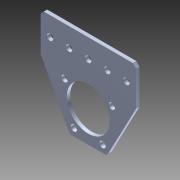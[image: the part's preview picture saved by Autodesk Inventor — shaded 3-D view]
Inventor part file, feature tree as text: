
AUTODESK INVENTOR PART (.ipt)
format: ipt  version: 2014 SP1 (Build 180222100, 222)  size: 152,576 bytes
history: native  units: in
note: dims shown in document units (in); Inventor stores cm internally (conversion verified against a paired STEP export)
features: other x2, sketch x1, imported_body x1
ambient origin geometry x8: Origin, YZ Plane, XZ Plane, XY Plane, X Axis, Y Axis, Z Axis, Center Point
bodies: Body1 (feature_tree)
feature tree (4):
  other  "Cut-Extrude1"
  other  "217-3553-STEP1"
  sketch  "Sketch1"
  imported_body  "Base1"
